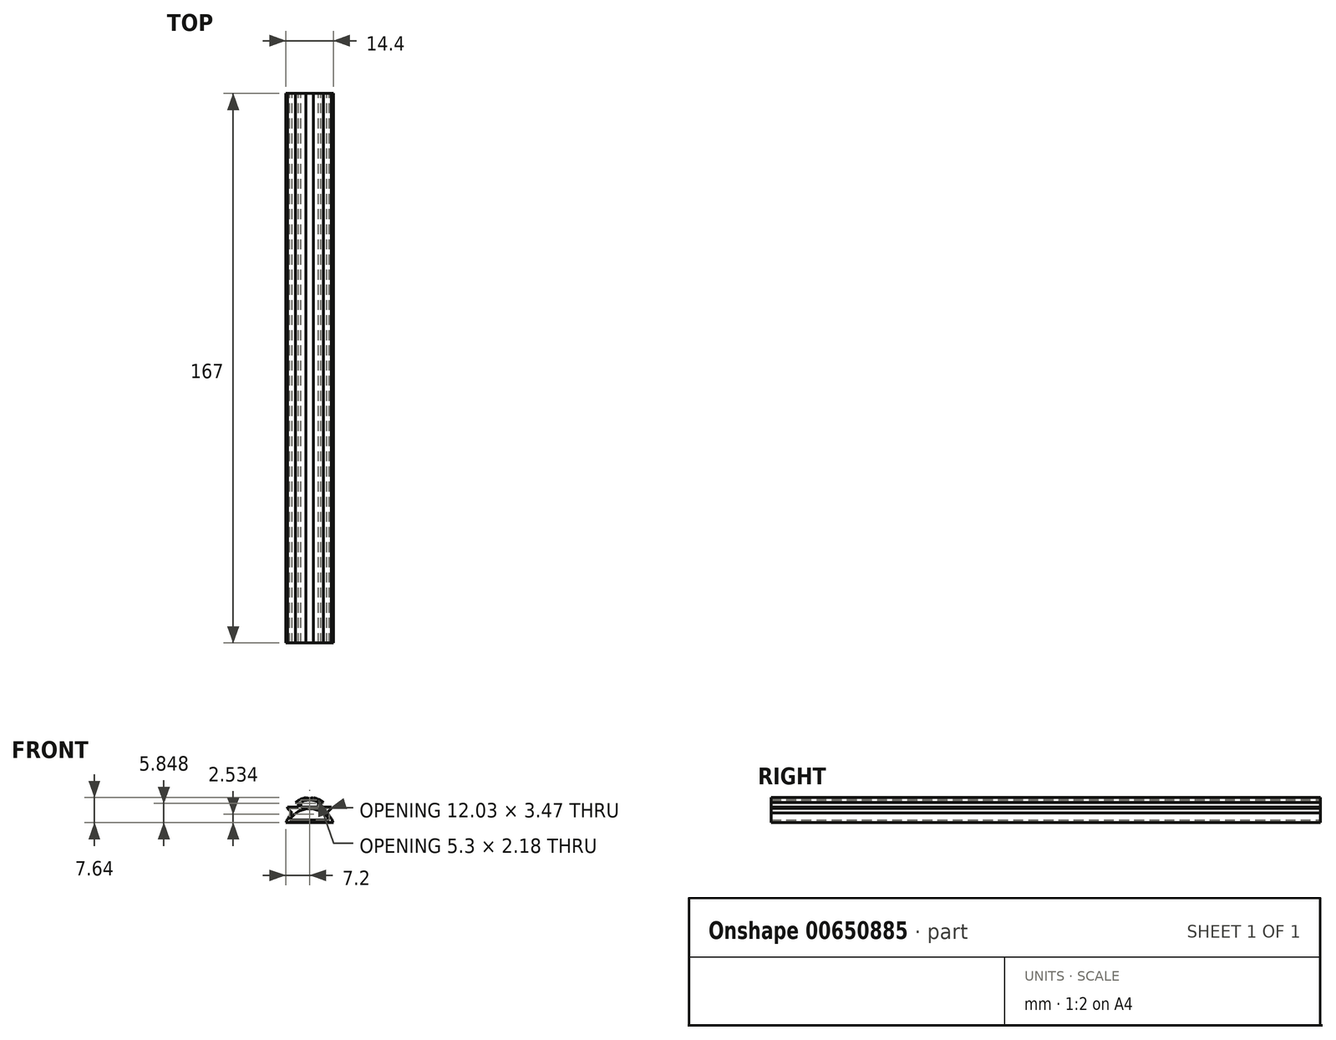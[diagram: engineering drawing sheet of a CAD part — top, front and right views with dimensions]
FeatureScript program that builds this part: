
annotation { "Feature Type Name" : "Feature", "Feature Type Description" : "" }
export const myFeature = defineFeature(function(context is Context, id is Id, definition is map)
    precondition{}
    {
        {
            var Q0;
            Q0=qCreatedBy(makeId("Front.planeOp"),FACE);
            var sketch = newSketch(context, id + "F0", { "sketchPlane" : qUnion([Q0])});
            skLineSegment(sketch, "E0", {"start": v(-7.2, 0) * mm, "end": v(7.2, 0) * mm});
            skLineSegment(sketch, "E1", {"start": v(-6.02, 0.8) * mm, "end": v(6.02, 0.8) * mm});
            skArc(sketch, "E2", {"start": v(6.02, 0.8) * mm, "mid": v(0, 4.27) * mm, "end": v(-6.02, 0.8) * mm});
            skLineSegment(sketch, "E3", {"start": v(6.65, 4.36) * mm, "end": v(6.65, 4.76) * mm});
            skLineSegment(sketch, "E4", {"start": v(-6.64, 4.76) * mm, "end": v(-6.65, 4.36) * mm});
            skLineSegment(sketch, "E5", {"start": v(6.65, 4.36) * mm, "end": v(5.25, 2.93) * mm});
            skLineSegment(sketch, "E6.MirrorCS", {"start": v(-6.65, 4.36) * mm, "end": v(-5.25, 2.93) * mm});
            skArc(sketch, "E7", {"start": v(-5.25, 2.93) * mm, "mid": v(-6.4, 1.58) * mm, "end": v(-7.2, 0) * mm});
            skArc(sketch, "E8", {"start": v(7.2, 0) * mm, "mid": v(6.4, 1.58) * mm, "end": v(5.25, 2.93) * mm});
            skLineSegment(sketch, "E9.left", {"start": v(-3.45, 6.16) * mm, "end": v(-3.45, 4.76) * mm});
            skLineSegment(sketch, "E9.right", {"start": v(3.45, 6.16) * mm, "end": v(3.45, 4.76) * mm});
            skLineSegment(sketch, "E10", {"start": v(-6.64, 4.76) * mm, "end": v(-3.45, 4.76) * mm});
            skLineSegment(sketch, "E11", {"start": v(6.65, 4.76) * mm, "end": v(3.45, 4.76) * mm});
            skLineSegment(sketch, "E12", {"start": v(3.45, 6.16) * mm, "end": v(4.25, 6.16) * mm});
            skLineSegment(sketch, "E13.MirrorCS", {"start": v(-3.45, 6.16) * mm, "end": v(-4.25, 6.16) * mm});
            skLineSegment(sketch, "E14.bottom", {"start": v(-2.65, 4.76) * mm, "end": v(2.65, 4.76) * mm});
            skLineSegment(sketch, "E14.left", {"start": v(-2.65, 4.76) * mm, "end": v(-2.65, 6.22) * mm});
            skLineSegment(sketch, "E14.right", {"start": v(2.65, 4.76) * mm, "end": v(2.65, 6.22) * mm});
            skLineSegment(sketch, "E15", {"start": v(-3.45, 4.76) * mm, "end": v(3.45, 4.76) * mm, "construction": true});
            skArc(sketch, "E16", {"start": v(2.65, 6.22) * mm, "mid": v(0, 6.94) * mm, "end": v(-2.65, 6.22) * mm});
            skArc(sketch, "E17", {"start": v(-1.14, 7.64) * mm, "mid": v(-2.78, 7.08) * mm, "end": v(-4.25, 6.16) * mm});
            skArc(sketch, "E18.MirrorCS", {"start": v(1.14, 7.64) * mm, "mid": v(2.78, 7.08) * mm, "end": v(4.25, 6.16) * mm});
            skArc(sketch, "E19", {"start": v(-1.14, 7.64) * mm, "mid": v(0, 7.42) * mm, "end": v(1.14, 7.64) * mm});
            skSolve(sketch);
        }
        {
            var Q0;
            Q0=makeQuery(id+"F0.imprint","IMPRINT",FACE,{"disambiguationData":[TD([[makeQuery(id+"F0.imprint","IMPRINT",EDGE,{"derivedFrom":sQuery(id+"F0.wireOp",EDGE,"E0")}),1.0]])]});
            extrude(context, id + "F1", {"entities" : qUnion([Q0]), "flatOperationType" : FlatOperationType.REMOVE, "depth" : 167 * mm, "offsetDistance" : 25 * mm, "domain" : OperationDomain.MODEL});
        }
    });
